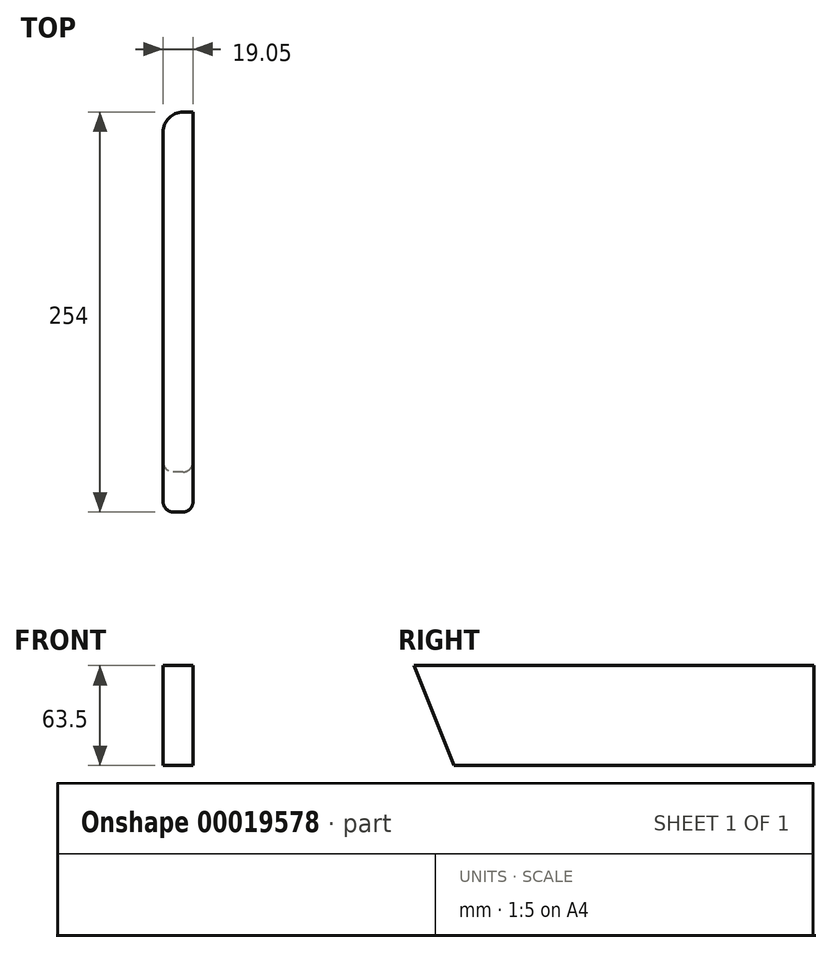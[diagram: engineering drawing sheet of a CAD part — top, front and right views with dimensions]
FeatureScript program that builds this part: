
annotation { "Feature Type Name" : "Feature", "Feature Type Description" : "" }
export const myFeature = defineFeature(function(context is Context, id is Id, definition is map)
    precondition{}
    {
        {
            var Q0;
            Q0=qCreatedBy(makeId("Right.planeOp"),FACE);
            var sketch = newSketch(context, id + "F0", { "sketchPlane" : qUnion([Q0])});
            skLineSegment(sketch, "E0", {"start": v(0, 0) * mm, "end": v(0, 63.5) * mm});
            skLineSegment(sketch, "E1", {"start": v(0, 63.5) * mm, "end": v(-254, 63.5) * mm});
            skLineSegment(sketch, "E2", {"start": v(-254, 63.5) * mm, "end": v(-228.6, 0) * mm});
            skLineSegment(sketch, "E3", {"start": v(-228.6, 0) * mm, "end": v(0, 0) * mm});
            skSolve(sketch);
        }
        {
            var Q0;
            Q0=makeQuery(id+"F0.imprint","IMPRINT",FACE,{"disambiguationData":[TD([[makeQuery(id+"F0.imprint","IMPRINT",EDGE,{"derivedFrom":sQuery(id+"F0.wireOp",EDGE,"E0")}),1.0]])]});
            extrude(context, id + "F1", {"entities" : qUnion([Q0]), "depth" : 19.05 * mm});
        }
        {
            var Q0;
            Q0=makeQuery(id+"F1.opExtrude","CAP_EDGE",EDGE,{"disambiguationData":[OSD([sQuery(id+"F0.wireOp",EDGE,"E2")])],"isStart":true});
            var Q1;
            Q1=makeQuery(id+"F1.opExtrude","CAP_EDGE",EDGE,{"disambiguationData":[OSD([sQuery(id+"F0.wireOp",EDGE,"E2")])],"isStart":false});
            fillet(context, id + "F2", {"entities" : qUnion([Q0, Q1]), "radius" : 6.35 * mm, "tangentPropagation" : true, "allowEdgeOverflow" : false});
        }
        {
            var Q0;
            Q0=makeQuery(id+"F1.opExtrude","CAP_EDGE",EDGE,{"disambiguationData":[OSD([sQuery(id+"F0.wireOp",EDGE,"E0")])],"isStart":true});
            fillet(context, id + "F3", {"entities" : qUnion([Q0]), "radius" : 12.7 * mm, "tangentPropagation" : true, "allowEdgeOverflow" : false});
        }
    });
